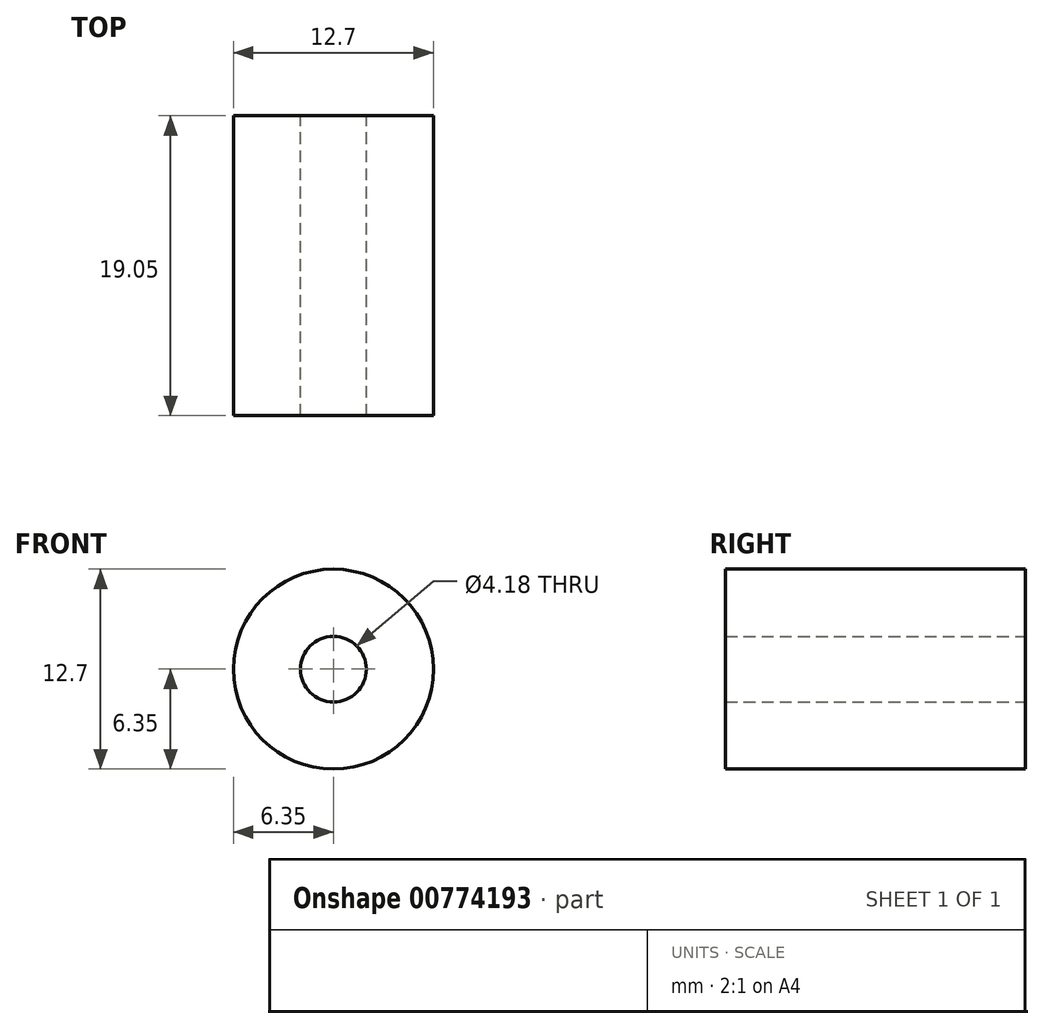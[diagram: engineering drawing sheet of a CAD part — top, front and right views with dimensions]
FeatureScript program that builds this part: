
annotation { "Feature Type Name" : "Feature", "Feature Type Description" : "" }
export const myFeature = defineFeature(function(context is Context, id is Id, definition is map)
    precondition{}
    {
        {
            var Q0;
            Q0=qCreatedBy(makeId("Front.planeOp"),FACE);
            var sketch = newSketch(context, id + "F0", { "sketchPlane" : qUnion([Q0])});
            skCircle(sketch, "E0", {"center": v(0, 0) * mm, "radius": 6.35 * mm});
            skCircle(sketch, "E1", {"center": v(0, 0) * mm, "radius": 2.1 * mm});
            skSolve(sketch);
        }
        {
            var Q0;
            Q0=makeQuery(id+"F0.imprint","IMPRINT",FACE,{"disambiguationData":[TD([[makeQuery(id+"F0.imprint","IMPRINT",EDGE,{"derivedFrom":sQuery(id+"F0.wireOp",EDGE,"E0")}),1.0]])]});
            extrude(context, id + "F1", {"entities" : qUnion([Q0]), "depth" : 19.05 * mm, "offsetDistance" : 25.4 * mm});
        }
    });
